# Revit family: QF_COMENDA_6C1121 Z
name_source: partatom
category: Attrezzature speciali
units: mm (PartAtom-declared; Revit-internal decimal feet)

## family parameters
Basato su piano di lavoro = No
Condiviso = No
Numero OmniClass = 23.40.40.14
Punto di calcolo locali = No
Quota connettore circolare = Usa diametro
Sempre verticale = Sì
Taglio con vuoti quando caricato = No
Tipo di parte = Normale
Titolo OmniClass = Food Service Equipment

## types (1)
- 6C1121/Z
    Altezza = 1520 mm
    Altezza allacciamento elettrico da pavimento finito = 160 mm  [stored 0.524934 ft]
    Altezza da terra raccordo acqua calda = 210 mm  [stored 0.688976 ft]
    Altezza dello scarico diretto acqua da pavimento finito = 160 mm  [stored 0.524934 ft]
    Corrente di funzionamento normale = 21 A
    Descrizione = MULTIPOWER HOOD SINGLE DISH DISHWASHER WITH HR PUMP, PERISTALTIC DOSING UNITS AND RCD
    Diametro dello scarico diretto di acqua = 1 1/2"
    Diametro raccordo acqua calda = 1"
    Fase = 3
    Frequenza = 50 Hz
    Lunghezza = 625 mm  [stored 2.05052 ft]
    Modello = TC10 R
    Numero dei poli = 3
    Peso netto = 118.00 kg
    Potenza elettrica = 14100 W
    Pressione minima acqua calda = 2000.0 Pa
    Produttore = COMENDA
    Profondità = 740 mm  [stored 2.42782 ft]
    Prospetto di default = 0 mm  [stored 0 ft]
    Protezione contro le sovracorrenti = 25 A
    Temperatura raccomandata per acqua calda = 50 °C
    Tensione = 400 V
    URL = www.comenda.eu
    URL catalogo = https://comenda.eu

note: [stored X ft] marks values corroborated as IEEE doubles in the binary element streams (Revit-internal decimal feet)

## geometry (parser evidence)
native form markers: Sweep x2
no freeform markers — native parametric forms only
